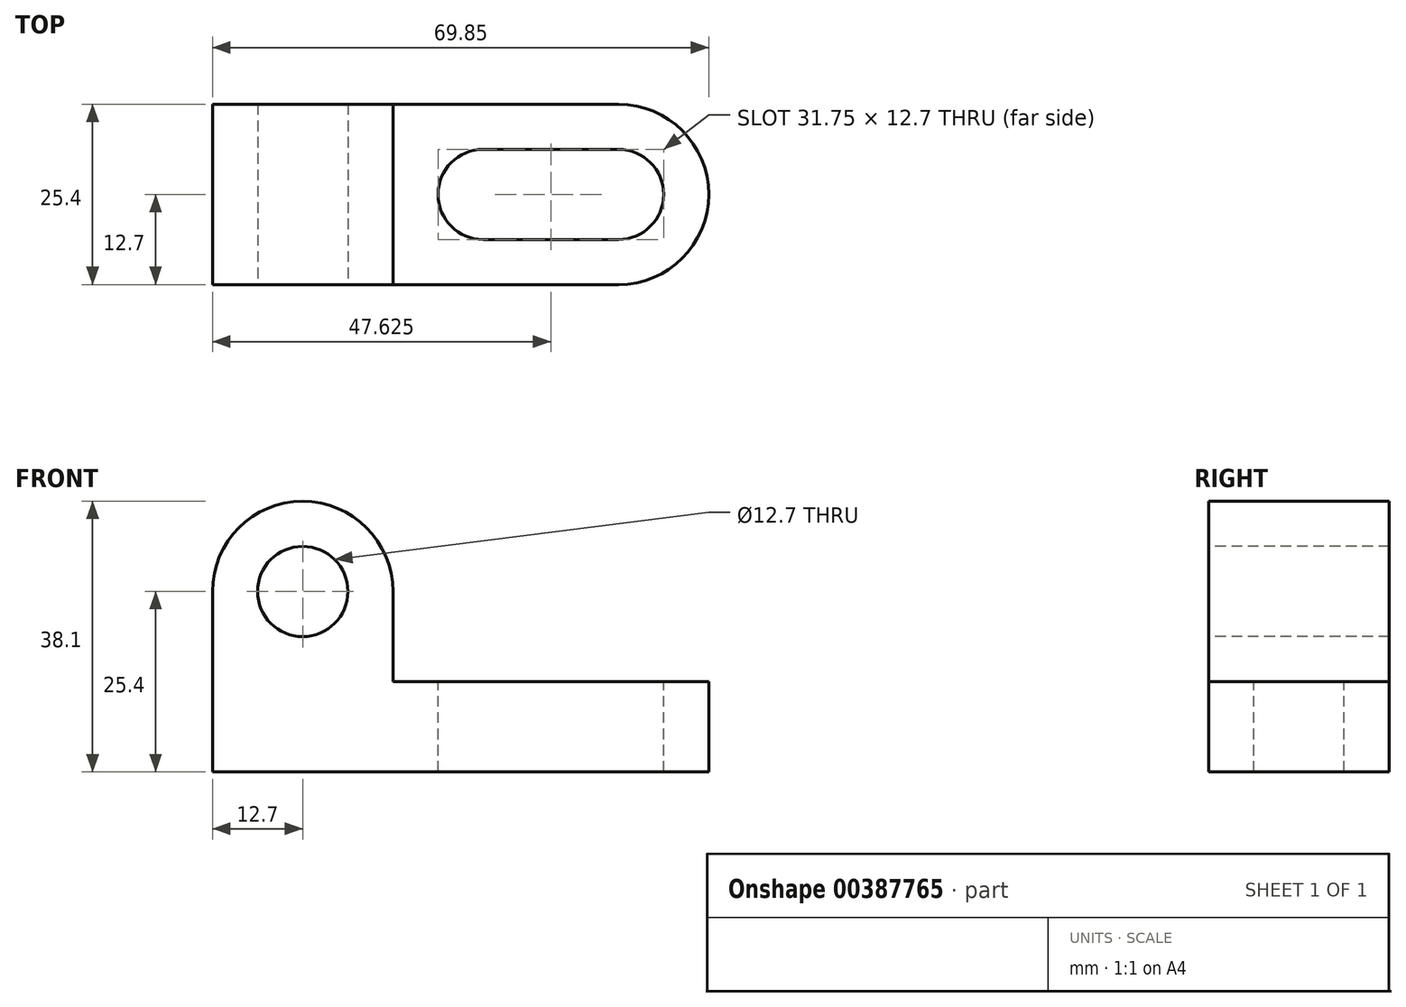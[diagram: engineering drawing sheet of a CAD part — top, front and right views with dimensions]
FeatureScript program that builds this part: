
annotation { "Feature Type Name" : "Feature", "Feature Type Description" : "" }
export const myFeature = defineFeature(function(context is Context, id is Id, definition is map)
    precondition{}
    {
        {
            var Q0;
            Q0=qCreatedBy(makeId("Front.planeOp"),FACE);
            var sketch = newSketch(context, id + "F0", { "sketchPlane" : qUnion([Q0])});
            skLineSegment(sketch, "E0", {"start": v(0, 0) * mm, "end": v(69.85, 0) * mm});
            skLineSegment(sketch, "E1", {"start": v(69.85, 0) * mm, "end": v(69.85, 12.7) * mm});
            skLineSegment(sketch, "E2", {"start": v(69.85, 12.7) * mm, "end": v(25.4, 12.7) * mm});
            skLineSegment(sketch, "E3", {"start": v(25.4, 12.7) * mm, "end": v(25.4, 38.1) * mm});
            skLineSegment(sketch, "E4", {"start": v(25.4, 38.1) * mm, "end": v(0, 38.1) * mm});
            skLineSegment(sketch, "E5", {"start": v(0, 38.1) * mm, "end": v(0, 0) * mm});
            skSolve(sketch);
        }
        {
            var Q0;
            Q0 = qSketchRegion(id + "F0", true);
            extrude(context, id + "F1", {"entities" : qUnion([Q0]), "depth" : 25.4 * mm});
        }
        {
            var Q0;
            Q0=makeQuery(id+"F1.opExtrude","CAP_FACE",FACE,{"disambiguationData":[OSD([sQuery(id+"F0.wireOp",EDGE,"E0"),sQuery(id+"F0.wireOp",EDGE,"E1"),sQuery(id+"F0.wireOp",EDGE,"E2"),sQuery(id+"F0.wireOp",EDGE,"E3"),sQuery(id+"F0.wireOp",EDGE,"E4"),sQuery(id+"F0.wireOp",EDGE,"E5")])],"isStart":false});
            var sketch = newSketch(context, id + "F2", { "sketchPlane" : qUnion([Q0])});
            skArc(sketch, "E6", {"start": v(25.4, 25.4) * mm, "mid": v(12.7, 38.1) * mm, "end": v(0, 25.4) * mm});
            skSolve(sketch);
        }
        {
            var Q0;
            {var subQ0=sQuery(id+"F2.wireOp",EDGE,"E6");var subQ1=makeQuery(id+"F1.opExtrude","CAP_EDGE",EDGE,{"disambiguationData":[OSD([sQuery(id+"F0.wireOp",EDGE,"E3")])],"isStart":false});var subQ2=makeQuery(id+"F2.imprint","INTERSECT",VERTEX,{"derivedFrom":[subQ1,subQ0]});Q0=makeQuery(id+"F2.imprint","IMPRINT",FACE,{"disambiguationData":[TD([[makeQuery(id+"F2.imprint","IMPRINT",EDGE,{"disambiguationData":[TD([[subQ2,-1.0]])],"derivedFrom":subQ0}),-1.0]])]});}
            var Q1;
            {var subQ0=sQuery(id+"F2.wireOp",EDGE,"E6");var subQ1=makeQuery(id+"F1.opExtrude","CAP_EDGE",EDGE,{"disambiguationData":[OSD([sQuery(id+"F0.wireOp",EDGE,"E5")])],"isStart":false});var subQ2=makeQuery(id+"F2.imprint","INTERSECT",VERTEX,{"derivedFrom":[subQ1,subQ0]});Q1=makeQuery(id+"F2.imprint","IMPRINT",FACE,{"disambiguationData":[TD([[makeQuery(id+"F2.imprint","IMPRINT",EDGE,{"disambiguationData":[TD([[subQ2,1.0]])],"derivedFrom":subQ0}),-1.0]])]});}
            extrude(context, id + "F3", {"entities" : qUnion([Q0, Q1]), "operationType" : NewBodyOperationType.REMOVE, "oppositeDirection" : true, "depth" : 25.4 * mm});
        }
        {
            var Q0;
            Q0=makeQuery(id+"F1.opExtrude","CAP_FACE",FACE,{"disambiguationData":[OSD([sQuery(id+"F0.wireOp",EDGE,"E0"),sQuery(id+"F0.wireOp",EDGE,"E1"),sQuery(id+"F0.wireOp",EDGE,"E2"),sQuery(id+"F0.wireOp",EDGE,"E3"),sQuery(id+"F0.wireOp",EDGE,"E4"),sQuery(id+"F0.wireOp",EDGE,"E5")])],"isStart":false});
            var sketch = newSketch(context, id + "F4", { "sketchPlane" : qUnion([Q0])});
            skCircle(sketch, "E7", {"center": v(12.7, 25.4) * mm, "radius": 6.35 * mm});
            skSolve(sketch);
        }
        {
            var Q0;
            Q0=makeQuery(id+"F4.imprint","IMPRINT",FACE,{"disambiguationData":[TD([[makeQuery(id+"F4.imprint","IMPRINT",EDGE,{"derivedFrom":sQuery(id+"F4.wireOp",EDGE,"E7")}),1.0]])]});
            extrude(context, id + "F5", {"entities" : qUnion([Q0]), "operationType" : NewBodyOperationType.REMOVE, "oppositeDirection" : true, "depth" : 25.4 * mm});
        }
        {
            var Q0;
            Q0=makeQuery(id+"F1.opExtrude","SWEPT_FACE",FACE,{"disambiguationData":[OSD([sQuery(id+"F0.wireOp",EDGE,"E2")])]});
            var sketch = newSketch(context, id + "F6", { "sketchPlane" : qUnion([Q0])});
            skCircle(sketch, "E8", {"center": v(38.1, -12.7) * mm, "radius": 6.35 * mm});
            skCircle(sketch, "E9", {"center": v(57.15, -12.7) * mm, "radius": 6.35 * mm});
            skPoint(sketch, "E9.centerSnap0", {"position": v(69.85, -12.7) * mm});
            skLineSegment(sketch, "E10", {"start": v(38.1, -6.35) * mm, "end": v(57.15, -6.35) * mm});
            skLineSegment(sketch, "E11", {"start": v(38.1, -19.05) * mm, "end": v(57.15, -19.05) * mm});
            skSolve(sketch);
        }
        {
            var Q0;
            {var subQ0=sQuery(id+"F6.wireOp",EDGE,"E8");var subQ1=makeQuery(id+"F6.imprint","INTERSECT",VERTEX,{"derivedFrom":[subQ0,sQuery(id+"F6.wireOp",EDGE,"E10")]});Q0=makeQuery(id+"F6.imprint","IMPRINT",FACE,{"disambiguationData":[TD([[makeQuery(id+"F6.imprint","IMPRINT",EDGE,{"disambiguationData":[TD([[subQ1,-1.0]])],"derivedFrom":subQ0}),1.0]])]});}
            var Q1;
            {var subQ0=sQuery(id+"F6.wireOp",EDGE,"E9");var subQ1=makeQuery(id+"F6.imprint","INTERSECT",VERTEX,{"derivedFrom":[subQ0,sQuery(id+"F6.wireOp",EDGE,"E10")]});Q1=makeQuery(id+"F6.imprint","IMPRINT",FACE,{"disambiguationData":[TD([[makeQuery(id+"F6.imprint","IMPRINT",EDGE,{"disambiguationData":[TD([[subQ1,-1.0]])],"derivedFrom":subQ0}),1.0]])]});}
            var Q2;
            {var subQ0=sQuery(id+"F6.wireOp",EDGE,"E10");Q2=makeQuery(id+"F6.imprint","IMPRINT",FACE,{"disambiguationData":[TD([[makeQuery(id+"F6.imprint","IMPRINT",EDGE,{"derivedFrom":subQ0}),-1.0]])]});}
            extrude(context, id + "F7", {"entities" : qUnion([Q0, Q1, Q2]), "operationType" : NewBodyOperationType.REMOVE, "oppositeDirection" : true, "depth" : 25.4 * mm});
        }
        {
            var Q0;
            Q0=makeQuery(id+"F1.opExtrude","SWEPT_FACE",FACE,{"disambiguationData":[OSD([sQuery(id+"F0.wireOp",EDGE,"E2")])]});
            var sketch = newSketch(context, id + "F8", { "sketchPlane" : qUnion([Q0])});
            skArc(sketch, "E12", {"start": v(57.15, -25.4) * mm, "mid": v(69.85, -12.7) * mm, "end": v(57.15, 0) * mm});
            skSolve(sketch);
        }
        {
            var Q0;
            {var subQ0=sQuery(id+"F8.wireOp",EDGE,"E12");var subQ1=sQuery(id+"F0.wireOp",EDGE,"E2");var subQ2=makeQuery(id+"F1.opExtrude","CAP_EDGE",EDGE,{"disambiguationData":[OSD([subQ1])],"isStart":true});var subQ3=makeQuery(id+"F8.imprint","INTERSECT",VERTEX,{"derivedFrom":[subQ2,subQ0]});Q0=makeQuery(id+"F8.imprint","IMPRINT",FACE,{"disambiguationData":[TD([[makeQuery(id+"F8.imprint","IMPRINT",EDGE,{"disambiguationData":[TD([[subQ3,1.0]])],"derivedFrom":subQ0}),-1.0]])]});}
            var Q1;
            {var subQ0=sQuery(id+"F8.wireOp",EDGE,"E12");var subQ1=sQuery(id+"F0.wireOp",EDGE,"E2");var subQ2=makeQuery(id+"F1.opExtrude","CAP_EDGE",EDGE,{"disambiguationData":[OSD([subQ1])],"isStart":false});var subQ3=makeQuery(id+"F8.imprint","INTERSECT",VERTEX,{"derivedFrom":[subQ2,subQ0]});Q1=makeQuery(id+"F8.imprint","IMPRINT",FACE,{"disambiguationData":[TD([[makeQuery(id+"F8.imprint","IMPRINT",EDGE,{"disambiguationData":[TD([[subQ3,-1.0]])],"derivedFrom":subQ0}),-1.0]])]});}
            extrude(context, id + "F9", {"entities" : qUnion([Q0, Q1]), "operationType" : NewBodyOperationType.REMOVE, "oppositeDirection" : true, "depth" : 25.4 * mm});
        }
    });
